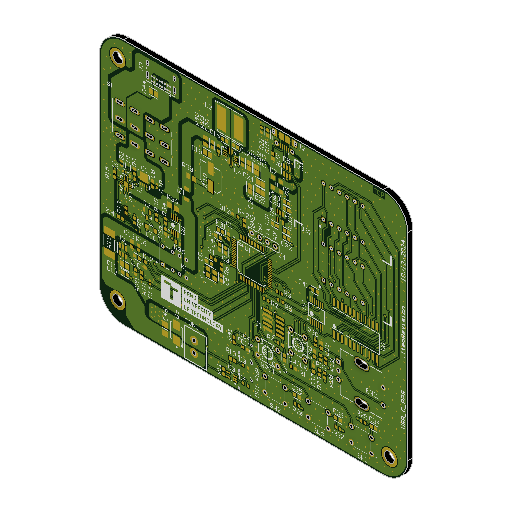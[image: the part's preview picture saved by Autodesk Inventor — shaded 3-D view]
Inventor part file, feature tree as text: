
AUTODESK INVENTOR PART (.ipt)
format: ipt  version: 2025 (Build 290162000, 162)  size: 2,440,704 bytes
history: native  units: in
note: dims shown in document units (in); Inventor stores cm internally (conversion verified against a paired STEP export)
features: sketch x121, hole x90, other x28, extrude x21
ambient origin geometry x8: Origin, YZ Plane, XZ Plane, XY Plane, X Axis, Y Axis, Z Axis, Center Point
bodies: Solid1 (feature_tree)
feature tree (260):
  other  "USB_C_PD_PPS_sink_BOARD"
  other  "BoardFrontPlane"
  extrude  "BoardOutline"  Depth=0.13in TaperAngle=0.0deg
  hole  "S2-4"  [1 undecoded]
  hole  "S2-3"  [1 undecoded]
  hole  "S2-2"  [1 undecoded]
  hole  "S2-1"  [1 undecoded]
  hole  "J4-1"  [1 undecoded]
  hole  "J4-4"  [1 undecoded]
  hole  "J4-3"  [1 undecoded]
  hole  "J4-2"  [1 undecoded]
  extrude  "S1-5"  Depth=0.13in TaperAngle=0.0deg
  extrude  "S1-2"  Depth=0.002in TaperAngle=0.0deg
  extrude  "S1-11"  Depth=0.002in TaperAngle=0.0deg
  extrude  "S1-8"  Depth=0.002in TaperAngle=0.0deg
  extrude  "S1-6"  Depth=0.002in TaperAngle=0.0deg
  extrude  "S1-3"  Depth=0.002in TaperAngle=0.0deg
  extrude  "S1-12"  Depth=0.0472in TaperAngle=0.0deg
  extrude  "S1-9"  [1 undecoded]
  extrude  "S1-7"  [1 undecoded]
  extrude  "S1-10"  [1 undecoded]
  extrude  "S1-1"  [1 undecoded]
  extrude  "S1-4"  [1 undecoded]
  hole  "K1-8"  [1 undecoded]
  hole  "K1-7"  [1 undecoded]
  hole  "K1-6"  [1 undecoded]
  hole  "K1-5"  [1 undecoded]
  hole  "K1-4"  [1 undecoded]
  hole  "K1-3"  [1 undecoded]
  hole  "K1-2"  [1 undecoded]
  hole  "K1-1"  [1 undecoded]
  extrude  "J3-3"  [1 undecoded]
  extrude  "J3-4"  [1 undecoded]
  extrude  "J3-1"  [1 undecoded]
  extrude  "J3-2"  [1 undecoded]
  hole  "J3-A1"  [1 undecoded]
  hole  "J3-A4"  [1 undecoded]
  hole  "J3-A5"  [1 undecoded]
  hole  "J3-A6"  [1 undecoded]
  hole  "J3-A7"  [1 undecoded]
  hole  "J3-A8"  [1 undecoded]
  hole  "J3-A9"  [1 undecoded]
  hole  "J3-A12"  [1 undecoded]
  hole  "J3-B1"  [1 undecoded]
  hole  "J3-B4"  [1 undecoded]
  hole  "J3-B5"  [1 undecoded]
  hole  "J3-B6"  [1 undecoded]
  hole  "J3-B7"  [1 undecoded]
  hole  "J3-B8"  [1 undecoded]
  hole  "J3-B9"  [1 undecoded]
  hole  "J3-B12"  [1 undecoded]
  hole  "J2-7"  [1 undecoded]
  hole  "J2-6"  [1 undecoded]
  extrude  "J2-11"  [1 undecoded]
  extrude  "J2-8"  [1 undecoded]
  hole  "ENC1-A"  [1 undecoded]
  hole  "ENC1-C"  [1 undecoded]
  hole  "ENC1-B"  [1 undecoded]
  extrude  "ENC1-3"  [1 undecoded]
  extrude  "ENC1-4"  [1 undecoded]
  hole  "ENC1-1"  [1 undecoded]
  hole  "ENC1-2"  [1 undecoded]
  hole  "DS2-7"  [1 undecoded]
  hole  "DS2-8"  [1 undecoded]
  hole  "DS2-9"  [1 undecoded]
  hole  "DS2-10"  [1 undecoded]
  hole  "DS2-11"  [1 undecoded]
  hole  "DS2-12"  [1 undecoded]
  hole  "DS2-1"  [1 undecoded]
  hole  "DS2-2"  [1 undecoded]
  hole  "DS2-3"  [1 undecoded]
  hole  "DS2-4"  [1 undecoded]
  hole  "DS2-5"  [1 undecoded]
  hole  "DS2-6"  [1 undecoded]
  hole  "DS1-7"  [1 undecoded]
  hole  "DS1-8"  [1 undecoded]
  hole  "DS1-9"  [1 undecoded]
  hole  "DS1-10"  [1 undecoded]
  hole  "DS1-11"  [1 undecoded]
  hole  "DS1-12"  [1 undecoded]
  hole  "DS1-1"  [1 undecoded]
  hole  "DS1-2"  [1 undecoded]
  hole  "DS1-3"  [1 undecoded]
  hole  "DS1-4"  [1 undecoded]
  hole  "DS1-5"  [1 undecoded]
  hole  "DS1-6"  [1 undecoded]
  hole  "Free-MH_UFFYUCRS"  [1 undecoded]
  hole  "Free-MH_NTYALDTJ"  [1 undecoded]
  hole  "Free-MH_SGBJWQGS"  [1 undecoded]
  hole  "LP3-TH_TUYHERHS_1"  [1 undecoded]
  hole  "LP3-TH_AGCPFLQI_1"  [1 undecoded]
  hole  "LP2-TH_TJIVDCAF_1"  [1 undecoded]
  hole  "LP2-TH_ARMWKDFP_1"  [1 undecoded]
  hole  "LP1-TH_UMCDBLLX_1"  [1 undecoded]
  hole  "LP1-TH_UEIXYMFC_1"  [1 undecoded]
  hole  "S3-4"  [1 undecoded]
  hole  "S3-3"  [1 undecoded]
  hole  "S3-2"  [1 undecoded]
  hole  "S3-1"  [1 undecoded]
  hole  "SW3-4"  [1 undecoded]
  hole  "SW3-3"  [1 undecoded]
  hole  "SW3-2"  [1 undecoded]
  hole  "SW3-1"  [1 undecoded]
  hole  "SW2-1"  [1 undecoded]
  hole  "SW2-2"  [1 undecoded]
  hole  "SW2-3"  [1 undecoded]
  hole  "SW2-4"  [1 undecoded]
  hole  "SW1-4"  [1 undecoded]
  hole  "SW1-3"  [1 undecoded]
  hole  "SW1-2"  [1 undecoded]
  hole  "SW1-1"  [1 undecoded]
  hole  "CON1-1"  [1 undecoded]
  hole  "CON1-2"  [1 undecoded]
  other  "Decal_Top"
  other  "Decal_Bottom"
  sketch  "Sketch1"  dims[d0=0.0624in d1=0.0in]
  sketch  "Sketch14"  dims[d76=0.0394in d77=0.75in d78=0.375in d79=0.25in d80=0.5635in d81=1.0in d82=0.0in]
  sketch  "Sketch15"  dims[d83=0.0394in d84=0.75in d85=0.375in d86=0.25in d87=0.5635in d88=1.0in d89=0.0in]
  sketch  "Sketch16"  dims[d90=0.0394in d91=0.75in d92=0.375in d93=0.25in d94=0.5635in d95=1.0in d96=0.0in]
  sketch  "Sketch17"  dims[d97=0.0394in d98=0.75in d99=0.375in d100=0.25in d101=0.5635in d102=1.0in d103=0.0in]
  sketch  "Sketch18"  dims[d104=0.0402in d105=0.75in d106=0.375in d107=0.25in d108=0.5635in d109=1.0in d110=0.0in]
  sketch  "Sketch19"  dims[d111=0.0402in d112=0.75in d113=0.375in d114=0.25in d115=0.5635in d116=1.0in d117=0.0in]
  sketch  "Sketch20"  dims[d118=0.0402in d119=0.75in d120=0.375in d121=0.25in d122=0.5635in d123=1.0in d124=0.0in]
  sketch  "Sketch21"  dims[d125=0.0402in d126=0.75in d127=0.375in d128=0.25in d129=0.5635in d130=1.0in d131=0.0in d216=0.13in d217=0.0in]
  sketch  "Sketch34"  dims[d218=0.13in d219=0.0in d220=0.13in d221=0.0in]
  sketch  "Sketch35"  dims[d222=0.13in d223=0.0in d224=0.13in d225=0.0in]
  sketch  "Sketch36"  dims[d226=0.13in d227=0.0in d228=0.13in d229=0.0in]
  sketch  "Sketch37"  dims[d230=0.13in d231=0.0in d232=0.13in d233=0.0in]
  sketch  "Sketch38"  dims[d234=0.13in d235=0.0in d236=0.13in d237=0.0in]
  sketch  "Sketch39"  dims[d238=0.13in d239=0.0in]
  sketch  "Sketch40"  dims[d240=0.0315in d241=0.75in d242=0.375in d243=0.25in d244=0.5635in d245=1.0in d246=0.0in]
  sketch  "Sketch41"  dims[d247=0.0315in d248=0.75in d249=0.375in d250=0.25in d251=0.5635in d252=1.0in d253=0.0in]
  sketch  "Sketch42"  dims[d254=0.0315in d255=0.75in d256=0.375in d257=0.25in d258=0.5635in d259=1.0in d260=0.0in]
  sketch  "Sketch43"  dims[d261=0.0315in d262=0.75in d263=0.375in d264=0.25in d265=0.5635in d266=1.0in d267=0.0in]
  sketch  "Sketch44"  dims[d268=0.0315in d269=0.75in d270=0.375in d271=0.25in d272=0.5635in d273=1.0in d274=0.0in]
  sketch  "Sketch45"  dims[d275=0.0315in d276=0.75in d277=0.375in d278=0.25in d279=0.5635in d280=1.0in d281=0.0in]
  sketch  "Sketch46"  dims[d282=0.0315in d283=0.75in d284=0.375in d285=0.25in d286=0.5635in d287=1.0in d288=0.0in]
  sketch  "Sketch47"  dims[d289=0.0315in d290=0.75in d291=0.375in d292=0.25in d293=0.5635in d294=1.0in d295=0.0in d296=0.13in d297=0.0in]
  sketch  "Sketch48"  dims[d298=0.13in d299=0.0in d300=0.13in d301=0.0in]
  sketch  "Sketch49"  dims[d302=0.13in d303=0.0in]
  sketch  "Sketch50"  dims[d304=0.0157in d305=0.75in d306=0.375in d307=0.25in d308=0.5635in d309=1.0in d310=0.0in]
  sketch  "Sketch51"  dims[d311=0.0157in d312=0.75in d313=0.375in d314=0.25in d315=0.5635in d316=1.0in d317=0.0in]
  sketch  "Sketch52"  dims[d318=0.0157in d319=0.75in d320=0.375in d321=0.25in d322=0.5635in d323=1.0in d324=0.0in]
  sketch  "Sketch53"  dims[d325=0.0157in d326=0.75in d327=0.375in d328=0.25in d329=0.5635in d330=1.0in d331=0.0in]
  sketch  "Sketch54"  dims[d332=0.0157in d333=0.75in d334=0.375in d335=0.25in d336=0.5635in d337=1.0in d338=0.0in]
  sketch  "Sketch55"  dims[d339=0.0157in d340=0.75in d341=0.375in d342=0.25in d343=0.5635in d344=1.0in d345=0.0in]
  sketch  "Sketch56"  dims[d346=0.0157in d347=0.75in d348=0.375in d349=0.25in d350=0.5635in d351=1.0in d352=0.0in]
  sketch  "Sketch57"  dims[d353=0.0157in d354=0.75in d355=0.375in d356=0.25in d357=0.5635in d358=1.0in d359=0.0in]
  sketch  "Sketch58"  dims[d360=0.0157in d361=0.75in d362=0.375in d363=0.25in d364=0.5635in d365=1.0in d366=0.0in]
  sketch  "Sketch59"  dims[d367=0.0157in d368=0.75in d369=0.375in d370=0.25in d371=0.5635in d372=1.0in d373=0.0in]
  sketch  "Sketch60"  dims[d374=0.0157in d375=0.75in d376=0.375in d377=0.25in d378=0.5635in d379=1.0in d380=0.0in]
  sketch  "Sketch61"  dims[d381=0.0157in d382=0.75in d383=0.375in d384=0.25in d385=0.5635in d386=1.0in d387=0.0in]
  sketch  "Sketch62"  dims[d388=0.0157in d389=0.75in d390=0.375in d391=0.25in d392=0.5635in d393=1.0in d394=0.0in]
  sketch  "Sketch63"  dims[d395=0.0157in d396=0.75in d397=0.375in d398=0.25in d399=0.5635in d400=1.0in d401=0.0in]
  sketch  "Sketch64"  dims[d402=0.0157in d403=0.75in d404=0.375in d405=0.25in d406=0.5635in d407=1.0in d408=0.0in]
  sketch  "Sketch65"  dims[d409=0.0157in d410=0.75in d411=0.375in d412=0.25in d413=0.5635in d414=1.0in d415=0.0in]
  sketch  "Sketch66"  dims[d416=0.0335in d417=0.75in d418=0.375in d419=0.25in d420=0.5635in d421=1.0in d422=0.0in]
  sketch  "Sketch67"  dims[d423=0.0335in d424=0.75in d425=0.375in d426=0.25in d427=0.5635in d428=1.0in d429=0.0in d430=0.13in d431=0.0in]
  sketch  "Sketch68"  dims[d432=0.13in d433=0.0in]
  sketch  "Sketch69"  dims[d434=0.0394in d435=0.75in d436=0.375in d437=0.25in d438=0.5635in d439=1.0in d440=0.0in]
  sketch  "Sketch70"  dims[d441=0.0394in d442=0.75in d443=0.375in d444=0.25in d445=0.5635in d446=1.0in d447=0.0in]
  sketch  "Sketch71"  dims[d448=0.0394in d449=0.75in d450=0.375in d451=0.25in d452=0.5635in d453=1.0in d454=0.0in d455=0.13in d456=0.0in]
  sketch  "Sketch72"  dims[d457=0.13in d458=0.0in]
  sketch  "Sketch73"  dims[d459=0.0394in d460=0.75in d461=0.375in d462=0.25in d463=0.5635in d464=1.0in d465=0.0in]
  sketch  "Sketch74"  dims[d466=0.0394in d467=0.75in d468=0.375in d469=0.25in d470=0.5635in d471=1.0in d472=0.0in]
  sketch  "Sketch75"  dims[d473=0.0295in d474=0.75in d475=0.375in d476=0.25in d477=0.5635in d478=1.0in d479=0.0in]
  sketch  "Sketch76"  dims[d480=0.0295in d481=0.75in d482=0.375in d483=0.25in d484=0.5635in d485=1.0in d486=0.0in]
  sketch  "Sketch77"  dims[d487=0.0295in d488=0.75in d489=0.375in d490=0.25in d491=0.5635in d492=1.0in d493=0.0in]
  sketch  "Sketch78"  dims[d494=0.0295in d495=0.75in d496=0.375in d497=0.25in d498=0.5635in d499=1.0in d500=0.0in]
  sketch  "Sketch79"  dims[d501=0.0295in d502=0.75in d503=0.375in d504=0.25in d505=0.5635in d506=1.0in d507=0.0in]
  sketch  "Sketch80"  dims[d508=0.0295in d509=0.75in d510=0.375in d511=0.25in d512=0.5635in d513=1.0in d514=0.0in]
  sketch  "Sketch81"  dims[d515=0.0295in d516=0.75in d517=0.375in d518=0.25in d519=0.5635in d520=1.0in d521=0.0in]
  sketch  "Sketch82"  dims[d522=0.0295in d523=0.75in d524=0.375in d525=0.25in d526=0.5635in d527=1.0in d528=0.0in]
  sketch  "Sketch83"  dims[d529=0.0295in d530=0.75in d531=0.375in d532=0.25in d533=0.5635in d534=1.0in d535=0.0in]
  sketch  "Sketch84"  dims[d536=0.0295in d537=0.75in d538=0.375in d539=0.25in d540=0.5635in d541=1.0in d542=0.0in]
  sketch  "Sketch85"  dims[d543=0.0295in d544=0.75in d545=0.375in d546=0.25in d547=0.5635in d548=1.0in d549=0.0in]
  sketch  "Sketch86"  dims[d550=0.0295in d551=0.75in d552=0.375in d553=0.25in d554=0.5635in d555=1.0in d556=0.0in]
  sketch  "Sketch87"  dims[d557=0.0295in d558=0.75in d559=0.375in d560=0.25in d561=0.5635in d562=1.0in d563=0.0in]
  sketch  "Sketch88"  dims[d564=0.0295in d565=0.75in d566=0.375in d567=0.25in d568=0.5635in d569=1.0in d570=0.0in]
  sketch  "Sketch89"  dims[d571=0.0295in d572=0.75in d573=0.375in d574=0.25in d575=0.5635in d576=1.0in d577=0.0in]
  sketch  "Sketch90"  dims[d578=0.0295in d579=0.75in d580=0.375in d581=0.25in d582=0.5635in d583=1.0in d584=0.0in]
  sketch  "Sketch91"  dims[d585=0.0295in d586=0.75in d587=0.375in d588=0.25in d589=0.5635in d590=1.0in d591=0.0in]
  sketch  "Sketch92"  dims[d592=0.0295in d593=0.75in d594=0.375in d595=0.25in d596=0.5635in d597=1.0in d598=0.0in]
  sketch  "Sketch93"  dims[d599=0.0295in d600=0.75in d601=0.375in d602=0.25in d603=0.5635in d604=1.0in d605=0.0in]
  sketch  "Sketch94"  dims[d606=0.0295in d607=0.75in d608=0.375in d609=0.25in d610=0.5635in d611=1.0in d612=0.0in]
  sketch  "Sketch95"  dims[d613=0.0295in d614=0.75in d615=0.375in d616=0.25in d617=0.5635in d618=1.0in d619=0.0in]
  sketch  "Sketch96"  dims[d620=0.0295in d621=0.75in d622=0.375in d623=0.25in d624=0.5635in d625=1.0in d626=0.0in]
  sketch  "Sketch97"  dims[d627=0.0295in d628=0.75in d629=0.375in d630=0.25in d631=0.5635in d632=1.0in d633=0.0in]
  sketch  "Sketch98"  dims[d634=0.0295in d635=0.75in d636=0.375in d637=0.25in d638=0.5635in d639=1.0in d640=0.0in]
  sketch  "Sketch99"  dims[d655=0.126in d656=0.75in d657=0.375in d658=0.25in d659=0.5635in d660=1.0in d661=0.0in]
  sketch  "Sketch100"  dims[d662=0.126in d663=0.75in d664=0.375in d665=0.25in d666=0.5635in d667=1.0in d668=0.0in]
  sketch  "Sketch101"  dims[d669=0.126in d670=0.75in d671=0.375in d672=0.25in d673=0.5635in d674=1.0in d675=0.0in d678=0.002in d679=0.0in]
  sketch  "Sketch102"  dims[d680=0.002in d681=0.0in d682=0.002in d683=0.0in]
  sketch  "Sketch103"  dims[d684=0.002in d685=0.0in d686=0.002in d687=0.0in]
  sketch  "Sketch104"  dims[d688=0.002in d689=0.0in d690=0.002in d691=0.0in]
  sketch  "Sketch105"  dims[d692=0.002in d693=0.0in d694=0.002in d695=0.0in]
  sketch  "Sketch106"  dims[d707=0.0244in d708=0.75in d709=0.375in d710=0.25in d711=0.5635in d712=1.0in d713=0.0in]
  sketch  "Sketch107"  dims[d721=0.0244in d722=0.75in d723=0.375in d724=0.25in d725=0.5635in d726=1.0in d727=0.0in]
  sketch  "Sketch108"  dims[d735=0.0244in d736=0.75in d737=0.375in d738=0.25in d739=0.5635in d740=1.0in d741=0.0in]
  sketch  "Sketch111"  dims[d749=0.0244in d750=0.75in d751=0.375in d752=0.25in d753=0.5635in d754=1.0in d755=0.0in]
  sketch  "Sketch112"  dims[d763=0.0244in d764=0.75in d765=0.375in d766=0.25in d767=0.5635in d768=1.0in d769=0.0in]
  sketch  "Sketch113"  dims[d777=0.0244in d778=0.75in d779=0.375in d780=0.25in d781=0.5635in d782=1.0in d783=0.0in]
  sketch  "Sketch115"  dims[d784=0.0394in d785=0.75in d786=0.375in d787=0.25in d788=0.5635in d789=1.0in d790=0.0in]
  other  "Srf2"
  sketch  "Sketch116"  dims[d791=0.0394in d792=0.75in d793=0.375in d794=0.25in d795=0.5635in d796=1.0in d797=0.0in]
  other  "Srf3"
  sketch  "Sketch117"  dims[d798=0.0394in d799=0.75in d800=0.375in d801=0.25in d802=0.5635in d803=1.0in d804=0.0in]
  other  "Srf4"
  sketch  "Sketch118"  dims[d805=0.0394in d806=0.75in d807=0.375in d808=0.25in d809=0.5635in d810=1.0in d811=0.0in]
  other  "Srf5"
  sketch  "Sketch119"  dims[d812=0.0413in d813=0.75in d814=0.375in d815=0.25in d816=0.5635in d817=1.0in d818=0.0in]
  other  "Srf6"
  sketch  "Sketch120"  dims[d819=0.0413in d820=0.75in d821=0.375in d822=0.25in d823=0.5635in d824=1.0in d825=0.0in]
  other  "Srf7"
  sketch  "Sketch121"  dims[d826=0.0413in d827=0.75in d828=0.375in d829=0.25in d830=0.5635in d831=1.0in d832=0.0in]
  other  "Srf8"
  sketch  "Sketch122"  dims[d833=0.0413in d834=0.75in d835=0.375in d836=0.25in d837=0.5635in d838=1.0in d839=0.0in]
  other  "Srf9"
  sketch  "Sketch123"  dims[d840=0.0413in d841=0.75in d842=0.375in d843=0.25in d844=0.5635in d845=1.0in d846=0.0in]
  other  "Srf10"
  sketch  "Sketch127"  dims[d847=0.0413in d848=0.75in d849=0.375in d850=0.25in d851=0.5635in d852=1.0in d853=0.0in]
  sketch  "Sketch129"  dims[d854=0.0413in d855=0.75in d856=0.375in d857=0.25in d858=0.5635in d859=1.0in d860=0.0in]
  sketch  "Sketch131"  dims[d861=0.0413in d862=0.75in d863=0.375in d864=0.25in d865=0.5635in d866=1.0in d867=0.0in]
  sketch  "Sketch133"  dims[d868=0.0413in d869=0.75in d870=0.375in d871=0.25in d872=0.5635in d873=1.0in d874=0.0in]
  sketch  "Sketch135"  dims[d875=0.0413in d876=0.75in d877=0.375in d878=0.25in d879=0.5635in d880=1.0in d881=0.0in]
  sketch  "Sketch137"  dims[d882=0.0413in d883=0.75in d884=0.375in d885=0.25in d886=0.5635in d887=1.0in d888=0.0in]
  sketch  "Sketch138"  dims[d889=0.0413in d890=0.75in d891=0.375in d892=0.25in d893=0.5635in d894=1.0in d895=0.0in]
  sketch  "Sketch139"  dims[d896=0.0472in d897=0.75in d898=0.375in d899=0.25in d900=0.5635in d901=1.0in d902=0.0in]
  sketch  "Sketch140"  dims[d903=0.0472in d904=0.75in d905=0.375in d906=0.25in d907=0.5635in d908=1.0in d909=0.0in d910=0.002in d911=0.0in]
  sketch  "Sketch141"  dims[d916=0.0624in d918=-0.0624in]
  sketch  "Sketch142"
  sketch  "Sketch143"
  sketch  "Sketch144"
  sketch  "Sketch145"
  sketch  "Sketch146"
  sketch  "Sketch147"
  sketch  "Sketch148"
  sketch  "Sketch149"
  sketch  "Sketch150"
  sketch  "Sketch151"
  sketch  "Sketch152"
  sketch  "Sketch153"
  sketch  "Sketch154"
  sketch  "Sketch155"
  sketch  "Sketch156"
  other  "Srf11"
  other  "img_Top"
  other  "G_-1352982981_TopDecalImage"
  other  "img_Bottom"
  other  "G_-1352982981_BottomDecalImage"
  other  "UI_BTNs"
  other  "U_Buck_boost"
  other  "MCU"
  other  "LOAD_SENSE"
  other  "Protection"
  other  "USB_B"
  other  "LDO"
  other  "Encoder"
  other  "OCP"
  other  "RoomDefinition"
note: 103 required parameter values undecoded (feature->parameter linkage not recoverable at this tier; creation-order binding heuristic only, values carry confidence <= 0.55)
